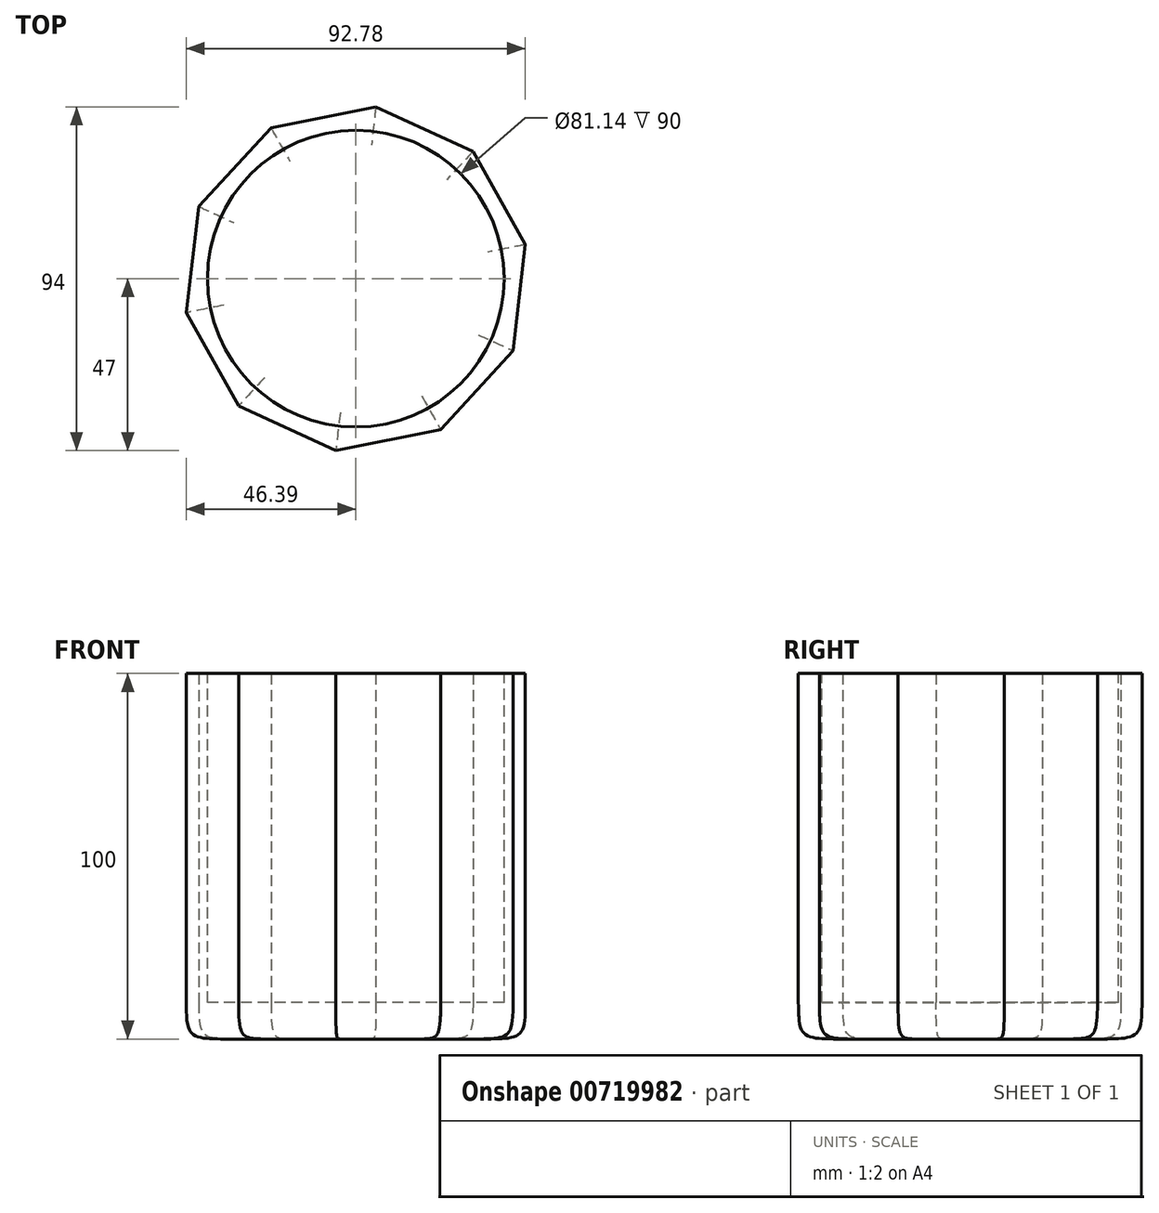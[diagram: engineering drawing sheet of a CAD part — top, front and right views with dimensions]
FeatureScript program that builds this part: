
annotation { "Feature Type Name" : "Feature", "Feature Type Description" : "" }
export const myFeature = defineFeature(function(context is Context, id is Id, definition is map)
    precondition{}
    {
        {
            var Q0;
            Q0=qCreatedBy(makeId("Top.planeOp"),FACE);
            var sketch = newSketch(context, id + "F0", { "sketchPlane" : qUnion([Q0])});
            skCircle(sketch, "E0.cCircle", {"center": v(0, 0) * mm, "radius": 45 * mm, "construction": true});
            skLineSegment(sketch, "E0.0", {"start": v(43, -19.73) * mm, "end": v(23.2, -41.24) * mm});
            skLineSegment(sketch, "E0.1", {"start": v(23.2, -41.24) * mm, "end": v(-5.47, -47) * mm});
            skLineSegment(sketch, "E0.2", {"start": v(-5.47, -47) * mm, "end": v(-32.05, -34.8) * mm});
            skLineSegment(sketch, "E0.3", {"start": v(-32.05, -34.8) * mm, "end": v(-46.39, -9.32) * mm});
            skLineSegment(sketch, "E0.4", {"start": v(-46.39, -9.32) * mm, "end": v(-43, 19.73) * mm});
            skLineSegment(sketch, "E0.5", {"start": v(-43, 19.73) * mm, "end": v(-23.2, 41.24) * mm});
            skLineSegment(sketch, "E0.6", {"start": v(-23.2, 41.24) * mm, "end": v(5.47, 47) * mm});
            skLineSegment(sketch, "E0.7", {"start": v(5.47, 47) * mm, "end": v(32.05, 34.8) * mm});
            skLineSegment(sketch, "E0.8", {"start": v(32.05, 34.8) * mm, "end": v(46.39, 9.32) * mm});
            skLineSegment(sketch, "E0.9", {"start": v(46.39, 9.32) * mm, "end": v(43, -19.73) * mm});
            skPoint(sketch, "E0.0.midPoint", {"position": v(33.1, -30.48) * mm});
            skSolve(sketch);
        }
        {
            var Q0;
            Q0=makeQuery(id+"F0.imprint","IMPRINT",FACE,{"disambiguationData":[TD([[makeQuery(id+"F0.imprint","IMPRINT",EDGE,{"derivedFrom":sQuery(id+"F0.wireOp",EDGE,"E0.0")}),-1.0]])]});
            extrude(context, id + "F1", {"entities" : qUnion([Q0]), "depth" : 100 * mm, "offsetDistance" : 25 * mm});
        }
        {
            var Q0;
            Q0=makeQuery(id+"F1.opExtrude","CAP_EDGE",EDGE,{"disambiguationData":[OSD([sQuery(id+"F0.wireOp",EDGE,"E0.6")])],"isStart":true});
            var Q1;
            Q1=makeQuery(id+"F1.opExtrude","CAP_EDGE",EDGE,{"disambiguationData":[OSD([sQuery(id+"F0.wireOp",EDGE,"E0.5")])],"isStart":true});
            var Q2;
            Q2=makeQuery(id+"F1.opExtrude","CAP_EDGE",EDGE,{"disambiguationData":[OSD([sQuery(id+"F0.wireOp",EDGE,"E0.4")])],"isStart":true});
            var Q3;
            Q3=makeQuery(id+"F1.opExtrude","CAP_EDGE",EDGE,{"disambiguationData":[OSD([sQuery(id+"F0.wireOp",EDGE,"E0.3")])],"isStart":true});
            var Q4;
            Q4=makeQuery(id+"F1.opExtrude","CAP_EDGE",EDGE,{"disambiguationData":[OSD([sQuery(id+"F0.wireOp",EDGE,"E0.2")])],"isStart":true});
            var Q5;
            Q5=makeQuery(id+"F1.opExtrude","CAP_EDGE",EDGE,{"disambiguationData":[OSD([sQuery(id+"F0.wireOp",EDGE,"E0.1")])],"isStart":true});
            var Q6;
            Q6=makeQuery(id+"F1.opExtrude","CAP_EDGE",EDGE,{"disambiguationData":[OSD([sQuery(id+"F0.wireOp",EDGE,"E0.0")])],"isStart":true});
            var Q7;
            Q7=makeQuery(id+"F1.opExtrude","CAP_EDGE",EDGE,{"disambiguationData":[OSD([sQuery(id+"F0.wireOp",EDGE,"E0.9")])],"isStart":true});
            var Q8;
            Q8=makeQuery(id+"F1.opExtrude","CAP_EDGE",EDGE,{"disambiguationData":[OSD([sQuery(id+"F0.wireOp",EDGE,"E0.8")])],"isStart":true});
            var Q9;
            Q9=makeQuery(id+"F1.opExtrude","CAP_EDGE",EDGE,{"disambiguationData":[OSD([sQuery(id+"F0.wireOp",EDGE,"E0.7")])],"isStart":true});
            fillet(context, id + "F2", {"entities" : qUnion([Q0, Q1, Q2, Q3, Q4, Q5, Q6, Q7, Q8, Q9]), "radius" : 10 * mm, "tangentPropagation" : true, "rho" : 0.7, "crossSection" : FilletCrossSection.CONIC, "allowEdgeOverflow" : false});
        }
        {
            var Q0;
            Q0=makeQuery(id+"F1.opExtrude","CAP_FACE",FACE,{"disambiguationData":[OSD([sQuery(id+"F0.wireOp",EDGE,"E0.0"),sQuery(id+"F0.wireOp",EDGE,"E0.1"),sQuery(id+"F0.wireOp",EDGE,"E0.2"),sQuery(id+"F0.wireOp",EDGE,"E0.3"),sQuery(id+"F0.wireOp",EDGE,"E0.4"),sQuery(id+"F0.wireOp",EDGE,"E0.5"),sQuery(id+"F0.wireOp",EDGE,"E0.6"),sQuery(id+"F0.wireOp",EDGE,"E0.7"),sQuery(id+"F0.wireOp",EDGE,"E0.8"),sQuery(id+"F0.wireOp",EDGE,"E0.9")])],"isStart":false});
            var sketch = newSketch(context, id + "F3", { "sketchPlane" : qUnion([Q0])});
            skCircle(sketch, "E1", {"center": v(0, 0) * mm, "radius": 40.57 * mm});
            skSolve(sketch);
        }
        {
            var Q0;
            Q0=makeQuery(id+"F3.imprint","IMPRINT",FACE,{"disambiguationData":[TD([[makeQuery(id+"F3.imprint","IMPRINT",EDGE,{"derivedFrom":sQuery(id+"F3.wireOp",EDGE,"E1")}),1.0]])]});
            extrude(context, id + "F4", {"entities" : qUnion([Q0]), "operationType" : NewBodyOperationType.REMOVE, "oppositeDirection" : true, "depth" : 90 * mm, "offsetDistance" : 25 * mm});
        }
    });
